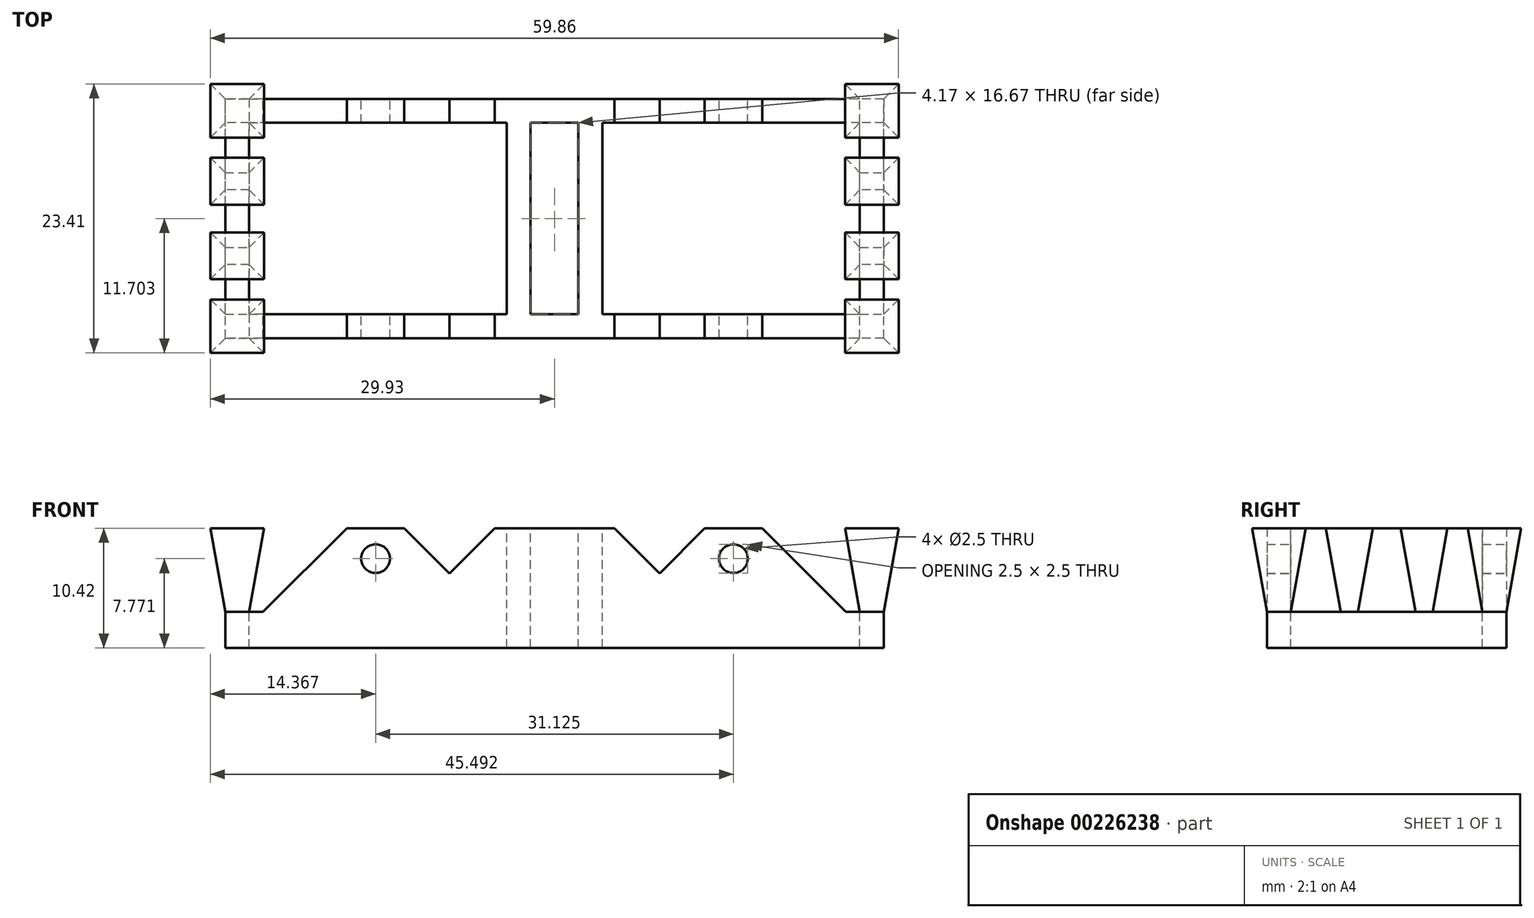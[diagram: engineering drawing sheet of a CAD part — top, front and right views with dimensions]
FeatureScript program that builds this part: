
annotation { "Feature Type Name" : "Feature", "Feature Type Description" : "" }
export const myFeature = defineFeature(function(context is Context, id is Id, definition is map)
    precondition{}
    {
        {
            var Q0;
            Q0=qCreatedBy(makeId("Front.planeOp"),FACE);
            var sketch = newSketch(context, id + "F0", { "sketchPlane" : qUnion([Q0])});
            skLineSegment(sketch, "E0", {"start": v(0, 0) * mm, "end": v(28.65, 0) * mm});
            skLineSegment(sketch, "E1", {"start": v(28.65, 0) * mm, "end": v(28.65, 3.13) * mm});
            skLineSegment(sketch, "E2", {"start": v(28.65, 3.13) * mm, "end": v(12.5, 3.12) * mm});
            skLineSegment(sketch, "E3", {"start": v(12.5, 3.12) * mm, "end": v(5.2, 10.42) * mm, "construction": true});
            skLineSegment(sketch, "E4", {"start": v(5.2, 10.42) * mm, "end": v(0, 10.42) * mm});
            skLineSegment(sketch, "E5", {"start": v(0, 10.42) * mm, "end": v(0, 0) * mm, "construction": true});
            skLineSegment(sketch, "E6", {"start": v(26.04, 3.13) * mm, "end": v(26.04, 0) * mm, "construction": true});
            skLineSegment(sketch, "E7", {"start": v(0, -2.7) * mm, "end": v(28.65, -2.7) * mm, "construction": true});
            skLineSegment(sketch, "E8", {"start": v(28.65, -2.7) * mm, "end": v(28.65, 0) * mm, "construction": true});
            skLineSegment(sketch, "E9", {"start": v(28.65, 3.13) * mm, "end": v(0, 3.13) * mm, "construction": true});
            skCircle(sketch, "E10", {"center": v(15.56, 7.77) * mm, "radius": 10.48 * mm, "construction": true});
            skPoint(sketch, "E11", {"position": v(14.32, 3.13) * mm});
            skLineSegment(sketch, "E12.MirrorCS", {"start": v(-28.65, 3.12) * mm, "end": v(-12.5, 3.12) * mm});
            skPoint(sketch, "E13.MirrorP", {"position": v(-14.32, 3.12) * mm});
            skLineSegment(sketch, "E14.MirrorCS", {"start": v(0, 0) * mm, "end": v(-28.65, 0) * mm});
            skCircle(sketch, "E15.MirrorC", {"center": v(-15.56, 7.77) * mm, "radius": 10.48 * mm, "construction": true});
            skLineSegment(sketch, "E16.MirrorCS", {"start": v(-26.04, 3.12) * mm, "end": v(-26.04, 0) * mm, "construction": true});
            skLineSegment(sketch, "E17.MirrorCS", {"start": v(-28.65, -2.7) * mm, "end": v(-28.65, 0) * mm, "construction": true});
            skLineSegment(sketch, "E18.MirrorCS", {"start": v(-28.65, 0) * mm, "end": v(-28.65, 3.12) * mm});
            skLineSegment(sketch, "E19.MirrorCS", {"start": v(-5.2, 10.42) * mm, "end": v(0, 10.42) * mm});
            skLineSegment(sketch, "E20.MirrorCS", {"start": v(0, -2.7) * mm, "end": v(-28.65, -2.7) * mm, "construction": true});
            skLineSegment(sketch, "E21.MirrorCS", {"start": v(-28.65, 3.12) * mm, "end": v(0, 3.13) * mm, "construction": true});
            skLineSegment(sketch, "E22.MirrorCS", {"start": v(-12.5, 3.12) * mm, "end": v(-5.2, 10.42) * mm, "construction": true});
            skCircle(sketch, "E23", {"center": v(15.56, 7.77) * mm, "radius": 1.25 * mm});
            skLineSegment(sketch, "E24", {"start": v(13.06, 10.42) * mm, "end": v(18.06, 10.42) * mm});
            skLineSegment(sketch, "E25", {"start": v(15.56, 7.77) * mm, "end": v(15.56, 10.42) * mm, "construction": true});
            skLineSegment(sketch, "E26.MirrorCS", {"start": v(-13.06, 10.42) * mm, "end": v(-18.06, 10.42) * mm});
            skCircle(sketch, "E27", {"center": v(-15.56, 7.77) * mm, "radius": 1.25 * mm});
            skLineSegment(sketch, "E28", {"start": v(13.06, 10.42) * mm, "end": v(9.14, 6.49) * mm});
            skLineSegment(sketch, "E29", {"start": v(-13.06, 10.42) * mm, "end": v(-9.14, 6.49) * mm});
            skLineSegment(sketch, "E30", {"start": v(-9.14, 6.49) * mm, "end": v(-5.2, 10.42) * mm});
            skLineSegment(sketch, "E31", {"start": v(5.2, 10.42) * mm, "end": v(9.14, 6.49) * mm});
            skLineSegment(sketch, "E32", {"start": v(18.06, 10.42) * mm, "end": v(25.35, 3.12) * mm});
            skLineSegment(sketch, "E33.MirrorCS", {"start": v(-18.06, 10.42) * mm, "end": v(-25.35, 3.12) * mm});
            skSolve(sketch);
        }
        {
            var Q0;
            Q0=qSketchRegion(id+"F0",true);
            extrude(context, id + "F1", {"entities" : qUnion([Q0]), "depth" : (1000 / 48) * mm});
        }
        {
            var Q0;
            Q0=makeQuery(id+"F1.opExtrude","SWEPT_FACE",FACE,{"disambiguationData":[OSD([sQuery(id+"F0.wireOp",EDGE,"E4"),sQuery(id+"F0.wireOp",EDGE,"E19.MirrorCS")])]});
            var sketch = newSketch(context, id + "F2", { "sketchPlane" : qUnion([Q0])});
            skLineSegment(sketch, "E34.bottom", {"start": v(-28.65, 0) * mm, "end": v(28.65, 0) * mm, "construction": true});
            skLineSegment(sketch, "E34.top", {"start": v(-28.65, -20.83) * mm, "end": v(28.65, -20.83) * mm, "construction": true});
            skLineSegment(sketch, "E34.left", {"start": v(-28.65, 0) * mm, "end": v(-28.65, -20.83) * mm, "construction": true});
            skLineSegment(sketch, "E34.right", {"start": v(28.65, 0) * mm, "end": v(28.65, -20.83) * mm, "construction": true});
            skLineSegment(sketch, "E35", {"start": v(-28.65, -2.08) * mm, "end": v(28.65, -2.08) * mm, "construction": true});
            skLineSegment(sketch, "E36", {"start": v(28.65, -2.08) * mm, "end": v(28.65, -18.75) * mm, "construction": true});
            skLineSegment(sketch, "E37", {"start": v(28.65, -18.75) * mm, "end": v(-28.65, -18.75) * mm, "construction": true});
            skLineSegment(sketch, "E38", {"start": v(-26.56, 0) * mm, "end": v(-26.56, -20.83) * mm, "construction": true});
            skLineSegment(sketch, "E39", {"start": v(26.56, 0) * mm, "end": v(26.56, -20.83) * mm, "construction": true});
            skLineSegment(sketch, "E40", {"start": v(-26.56, -2.08) * mm, "end": v(-4.17, -2.08) * mm});
            skLineSegment(sketch, "E41", {"start": v(-4.17, -2.08) * mm, "end": v(-4.17, -18.75) * mm});
            skLineSegment(sketch, "E42", {"start": v(-4.17, -18.75) * mm, "end": v(-26.56, -18.75) * mm});
            skLineSegment(sketch, "E43", {"start": v(-26.56, -18.75) * mm, "end": v(-26.56, -2.08) * mm});
            skLineSegment(sketch, "E44", {"start": v(4.17, -2.08) * mm, "end": v(26.56, -2.08) * mm});
            skLineSegment(sketch, "E45", {"start": v(26.56, -2.08) * mm, "end": v(26.56, -18.75) * mm});
            skLineSegment(sketch, "E46", {"start": v(26.56, -18.75) * mm, "end": v(4.17, -18.75) * mm});
            skLineSegment(sketch, "E47", {"start": v(4.17, -18.75) * mm, "end": v(4.17, -2.08) * mm});
            skLineSegment(sketch, "E48", {"start": v(0, 0) * mm, "end": v(0, -20.83) * mm, "construction": true});
            skLineSegment(sketch, "E49.bottom", {"start": v(-2.08, -2.08) * mm, "end": v(2.08, -2.08) * mm});
            skLineSegment(sketch, "E49.top", {"start": v(-2.08, -18.75) * mm, "end": v(2.08, -18.75) * mm});
            skLineSegment(sketch, "E49.left", {"start": v(-2.08, -2.08) * mm, "end": v(-2.08, -18.75) * mm});
            skLineSegment(sketch, "E49.right", {"start": v(2.08, -2.08) * mm, "end": v(2.08, -18.75) * mm});
            skSolve(sketch);
        }
        {
            var Q0;
            Q0=qSketchRegion(id+"F2",true);
            extrude(context, id + "F3", {"entities" : qUnion([Q0]), "operationType" : NewBodyOperationType.REMOVE, "endBound" : BoundingType.THROUGH_ALL, "oppositeDirection" : true, "depth" : 25 * mm});
        }
        {
            var Q0;
            {var subQ2=sQuery(id+"FkZIQYqMyQhmiDA_1.wireOp",EDGE,"n02PDE0u-Wzlv-NpWL-HXXN-utUJNTRTw1BJ");var subQ3=sQuery(id+"F0.wireOp",EDGE,"E12.MirrorCS");Q0=makeQuery(id+"FXX1ascl1I5hF3L_1.boolean.opBoolean","SPLIT",FACE,{"disambiguationData":[TD([makeQuery(id+"FXX1ascl1I5hF3L_1.opExtrude","SWEPT_FACE",FACE,{"disambiguationData":[OSD([subQ2])]})])],"derivedFrom":makeQuery(id+"F1.opExtrude","SWEPT_FACE",FACE,{"disambiguationData":[OSD([subQ3])]})});}
            cPlane(context, id + "F4", {"entities" : qUnion([Q0]), "cplaneType" : CPlaneType.OFFSET, "offset" : 0 * mm, "width" : 150 * mm, "height" : 150 * mm});
        }
        {
            var Q0;
            Q0=qCreatedBy(id+"F4.planeOp",FACE);
            var sketch = newSketch(context, id + "F5", { "sketchPlane" : qUnion([Q0])});
            skLineSegment(sketch, "E50.bottom", {"start": v(-28.65, 0) * mm, "end": v(28.65, 0) * mm, "construction": true});
            skLineSegment(sketch, "E50.top", {"start": v(-28.65, -20.83) * mm, "end": v(28.65, -20.83) * mm, "construction": true});
            skLineSegment(sketch, "E50.left", {"start": v(-28.65, 0) * mm, "end": v(-28.65, -20.83) * mm, "construction": true});
            skLineSegment(sketch, "E50.right", {"start": v(28.65, 0) * mm, "end": v(28.65, -20.83) * mm, "construction": true});
            skLineSegment(sketch, "E51.bottom", {"start": v(26.56, -18.75) * mm, "end": v(-26.56, -18.75) * mm, "construction": true});
            skLineSegment(sketch, "E51.top", {"start": v(26.56, -2.08) * mm, "end": v(-26.56, -2.08) * mm, "construction": true});
            skLineSegment(sketch, "E51.left", {"start": v(26.56, -18.75) * mm, "end": v(26.56, -2.08) * mm, "construction": true});
            skLineSegment(sketch, "E51.right", {"start": v(-26.56, -18.75) * mm, "end": v(-26.56, -2.08) * mm, "construction": true});
            skLineSegment(sketch, "E52.bottom", {"start": v(-28.65, 0) * mm, "end": v(-26.56, 0) * mm});
            skLineSegment(sketch, "E52.top", {"start": v(-28.65, -2.08) * mm, "end": v(-26.56, -2.08) * mm});
            skLineSegment(sketch, "E52.left", {"start": v(-28.65, 0) * mm, "end": v(-28.65, -2.08) * mm});
            skLineSegment(sketch, "E52.right", {"start": v(-26.56, 0) * mm, "end": v(-26.56, -2.08) * mm});
            skLineSegment(sketch, "E53.bottom", {"start": v(-26.56, -18.75) * mm, "end": v(-28.65, -18.75) * mm});
            skLineSegment(sketch, "E53.top", {"start": v(-26.56, -20.83) * mm, "end": v(-28.65, -20.83) * mm});
            skLineSegment(sketch, "E53.left", {"start": v(-26.56, -18.75) * mm, "end": v(-26.56, -20.83) * mm});
            skLineSegment(sketch, "E53.right", {"start": v(-28.65, -18.75) * mm, "end": v(-28.65, -20.83) * mm});
            skLineSegment(sketch, "E54.bottom", {"start": v(26.56, -2.08) * mm, "end": v(28.65, -2.08) * mm});
            skLineSegment(sketch, "E54.top", {"start": v(26.56, 0) * mm, "end": v(28.65, 0) * mm});
            skLineSegment(sketch, "E54.left", {"start": v(26.56, -2.08) * mm, "end": v(26.56, 0) * mm});
            skLineSegment(sketch, "E54.right", {"start": v(28.65, -2.08) * mm, "end": v(28.65, 0) * mm});
            skLineSegment(sketch, "E55.bottom", {"start": v(28.65, -20.83) * mm, "end": v(26.56, -20.83) * mm});
            skLineSegment(sketch, "E55.top", {"start": v(28.65, -18.75) * mm, "end": v(26.56, -18.75) * mm});
            skLineSegment(sketch, "E55.left", {"start": v(28.65, -20.83) * mm, "end": v(28.65, -18.75) * mm});
            skLineSegment(sketch, "E55.right", {"start": v(26.56, -20.83) * mm, "end": v(26.56, -18.75) * mm});
            skLineSegment(sketch, "E56", {"start": v(0, 0) * mm, "end": v(0, -20.83) * mm, "construction": true});
            skLineSegment(sketch, "E57.bottom", {"start": v(26.56, -7.92) * mm, "end": v(-26.56, -7.92) * mm, "construction": true});
            skLineSegment(sketch, "E57.top", {"start": v(26.56, -12.92) * mm, "end": v(-26.56, -12.92) * mm, "construction": true});
            skLineSegment(sketch, "E57.left", {"start": v(26.56, -7.92) * mm, "end": v(26.56, -12.92) * mm, "construction": true});
            skLineSegment(sketch, "E57.right", {"start": v(-26.56, -7.92) * mm, "end": v(-26.56, -12.92) * mm, "construction": true});
            skPoint(sketch, "E57.middle", {"position": v(0, -10.42) * mm});
            skLineSegment(sketch, "E58.bottom", {"start": v(26.56, -7.92) * mm, "end": v(28.65, -7.92) * mm});
            skLineSegment(sketch, "E58.top", {"start": v(26.56, -6.42) * mm, "end": v(28.65, -6.42) * mm});
            skLineSegment(sketch, "E58.left", {"start": v(26.56, -7.92) * mm, "end": v(26.56, -6.42) * mm});
            skLineSegment(sketch, "E58.right", {"start": v(28.65, -7.92) * mm, "end": v(28.65, -6.42) * mm});
            skLineSegment(sketch, "E59.bottom", {"start": v(26.56, -12.92) * mm, "end": v(28.65, -12.92) * mm});
            skLineSegment(sketch, "E59.top", {"start": v(26.56, -14.42) * mm, "end": v(28.65, -14.42) * mm});
            skLineSegment(sketch, "E59.left", {"start": v(26.56, -12.92) * mm, "end": v(26.56, -14.42) * mm});
            skLineSegment(sketch, "E59.right", {"start": v(28.65, -12.92) * mm, "end": v(28.65, -14.42) * mm});
            skLineSegment(sketch, "E60.bottom", {"start": v(-26.56, -7.92) * mm, "end": v(-28.65, -7.92) * mm});
            skLineSegment(sketch, "E60.top", {"start": v(-26.56, -6.42) * mm, "end": v(-28.65, -6.42) * mm});
            skLineSegment(sketch, "E60.left", {"start": v(-26.56, -7.92) * mm, "end": v(-26.56, -6.42) * mm});
            skLineSegment(sketch, "E60.right", {"start": v(-28.65, -7.92) * mm, "end": v(-28.65, -6.42) * mm});
            skLineSegment(sketch, "E61.bottom", {"start": v(-26.56, -12.92) * mm, "end": v(-28.65, -12.92) * mm});
            skLineSegment(sketch, "E61.top", {"start": v(-26.56, -14.42) * mm, "end": v(-28.65, -14.42) * mm});
            skLineSegment(sketch, "E61.left", {"start": v(-26.56, -12.92) * mm, "end": v(-26.56, -14.42) * mm});
            skLineSegment(sketch, "E61.right", {"start": v(-28.65, -12.92) * mm, "end": v(-28.65, -14.42) * mm});
            skSolve(sketch);
        }
        {
            var Q0;
            Q0 = qSketchRegion(id + "F5", true);
            var Q1;
            Q1=makeQuery(id+"F1.opExtrude","SWEPT_FACE",FACE,{"disambiguationData":[OSD([sQuery(id+"F0.wireOp",EDGE,"E4"),sQuery(id+"F0.wireOp",EDGE,"E19.MirrorCS")])]});
            extrude(context, id + "F6", {"entities" : qUnion([Q0]), "operationType" : NewBodyOperationType.ADD, "endBound" : BoundingType.UP_TO_SURFACE, "endBoundEntityFace" : qUnion([Q1]), "depth" : 25 * mm, "hasDraft" : true, "draftAngle" : 10 * degree});
        }
    });
